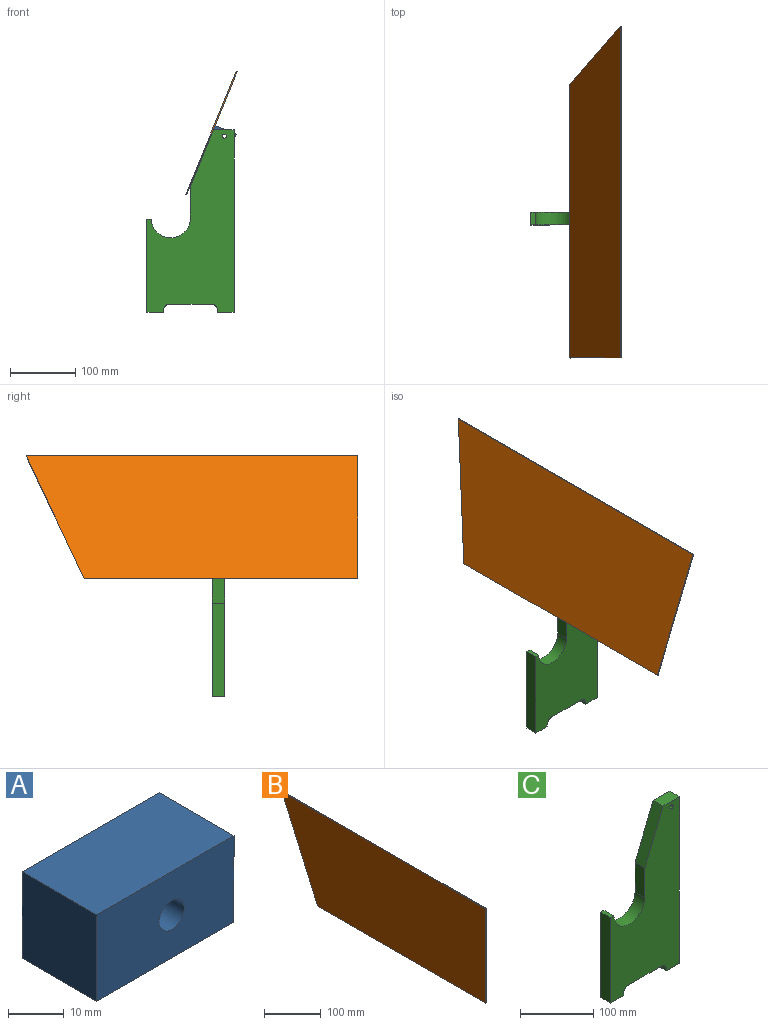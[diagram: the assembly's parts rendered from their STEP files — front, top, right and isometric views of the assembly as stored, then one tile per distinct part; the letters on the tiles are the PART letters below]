
ASSEMBLY  parts=3 mates=2
PART A: 7 faces, bbox 34.9x19.1x19.1 mm
  f0: plane 34.93x19.05mm, normal (0,0,-1), area 665.3mm2, adj f1,f3,f4,f5
  f1: plane 19.05x19.05mm, normal (1,0,0), area 362.9mm2, adj f0,f2,f4,f5
  f2: plane 34.93x19.05mm, normal (0,0,1), area 665.3mm2, adj f1,f3,f4,f5
  f3: plane 19.05x19.05mm, normal (-1,0,0), area 362.9mm2, adj f0,f2,f4,f5
  f4: plane 34.93x19.05mm, normal (0,-1,0), area 633.7mm2, adj f0,f1,f2,f3,f6
  f5: plane 34.93x19.05mm, normal (0,1,0), area 633.7mm2, adj f0,f1,f2,f3,f6
  f6: cylinder r=3.17mm len=19.05mm, axis (0,-1,0), area 380mm2, adj f4,f5
PART B: 6 faces, bbox 1.6x508x203.2 mm
  f0: plane 419.2x1.59mm, normal (0,0,-1), area 665.5mm2, adj f1,f3,f4,f5
  f1: plane 508x203.2mm, normal (1,0,0), area 94203.9mm2, adj f0,f2,f4,f5
  f2: plane 508x1.59mm, normal (0,0,1), area 806.5mm2, adj f1,f3,f4,f5
  f3: plane 508x203.2mm, normal (-1,0,0), area 94203.9mm2, adj f0,f2,f4,f5
  f4: plane 203.2x1.59mm, normal (0,-1,0), area 322.6mm2, adj f0,f1,f2,f3
  f5: plane 203.2x88.8mm, normal (0,0.92,-0.4), area 352mm2, adj f0,f1,f2,f3
PART C: 18 faces, bbox 133.4x19.1x279.4 mm
  f0: plane 19.05x6.39mm, normal (0,0,1), area 121.8mm2, adj f1,f8,f15,f17
  f1: plane 279.4x133.35mm, normal (0,1,0), area 24271.2mm2, adj f0,f2,f3,f4,f5,f6,f7,f8
  f2: plane 25.4x19.05mm, normal (0,0,-1), area 483.9mm2, adj f1,f3,f14,f15
  f3: plane 279.4x19.05mm, normal (1,0,0), area 5322.6mm2, adj f1,f2,f4,f15
  f4: plane 31.75x19.05mm, normal (0,0,1), area 604.8mm2, adj f1,f3,f5,f15
  f5: plane 86.44x34.93mm, normal (-0.93,0,0.37), area 1776.1mm2, adj f1,f4,f6,f15
  f6: plane 50.08x19.05mm, normal (-1,0,0), area 954.1mm2, adj f1,f5,f7,f15
  f7: plane 19.05x0.04mm, normal (0,0,1), area 0.8mm2, adj f1,f6,f15,f17
  f8: plane 142.88x19.05mm, normal (-1,0,0), area 2721.8mm2, adj f0,f1,f9,f15
  f9: plane 25.4x19.05mm, normal (0,0,-1), area 483.9mm2, adj f1,f8,f10,f15
  f10: plane 19.05x3.18mm, normal (1,0,0), area 60.5mm2, adj f1,f9,f11,f15
  f11: cylinder r=9.53mm len=19.05mm, axis (0,1,0), area 285mm2, adj f1,f10,f12,f15
  f12: plane 63.5x19.05mm, normal (0,0,-1), area 1209.7mm2, adj f1,f11,f13,f15
  f13: cylinder r=9.53mm len=19.05mm, axis (0,1,0), area 285mm2, adj f1,f12,f14,f15
  f14: plane 19.05x3.18mm, normal (-1,0,0), area 60.5mm2, adj f1,f2,f13,f15
  f15: plane 279.4x133.35mm, normal (0,-1,0), area 24271.2mm2, adj f0,f2,f3,f4,f5,f6,f7,f8
  f16: cylinder r=3.17mm len=19.05mm, axis (0,1,0), area 380mm2, adj f1,f15
  f17: cylinder r=30.16mm len=60.24mm, axis (0,1,0), area 1744.6mm2, adj f0,f1,f7,f15
PLACE A rot(axis=(0,1,0),22.3deg) t=(-3.97,19.05,255.04)mm
PLACE B rot(axis=(0,1,0),22.3deg) t=(-72.43,285.02,180.08)mm
PLACE C at identity fixed
MATE revolute A.f6 <-> C.f16  axis (0,-1,0) through (-15.05,0,269.87)mm
MATE fastened A.f3 <-> B.f1  axis (-0.93,0,0.38) through (-32.68,9.53,277.1)mm
